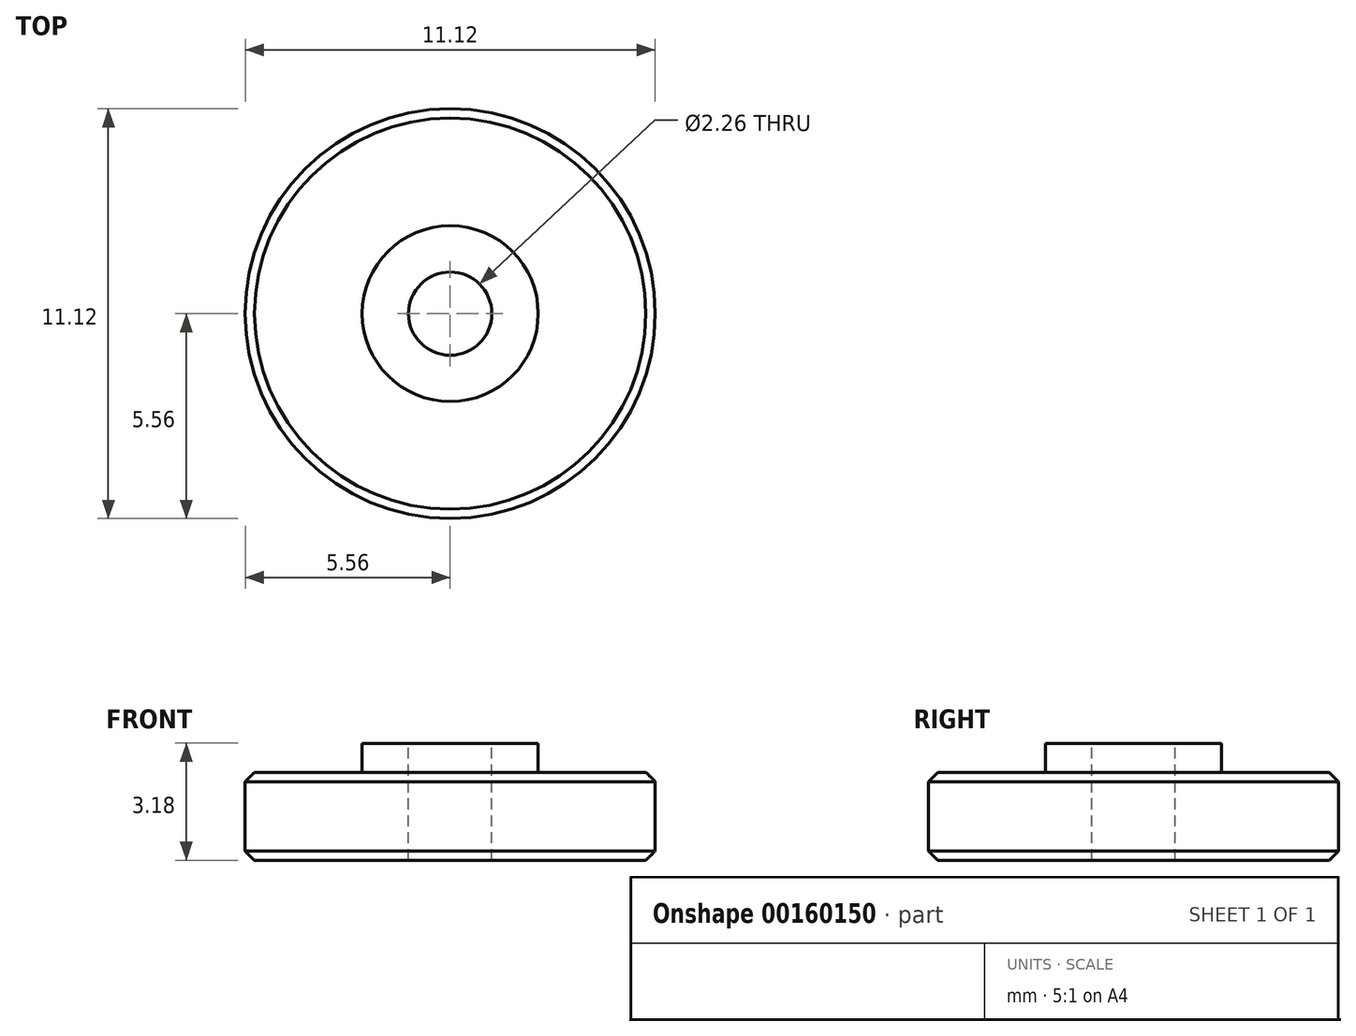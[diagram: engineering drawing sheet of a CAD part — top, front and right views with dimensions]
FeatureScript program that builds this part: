
annotation { "Feature Type Name" : "Feature", "Feature Type Description" : "" }
export const myFeature = defineFeature(function(context is Context, id is Id, definition is map)
    precondition{}
    {
        {
            var Q0;
            Q0=qCreatedBy(makeId("Top.planeOp"),FACE);
            var sketch = newSketch(context, id + "F0", { "sketchPlane" : qUnion([Q0])});
            skCircle(sketch, "E0", {"center": v(0, 0) * mm, "radius": 5.56 * mm});
            skSolve(sketch);
        }
        {
            var Q0;
            Q0 = qSketchRegion(id + "F0", true);
            extrude(context, id + "F1", {"entities" : qUnion([Q0]), "depth" : 2.4 * mm});
        }
        {
            var Q0;
            Q0=makeQuery(id+"F1.opExtrude","CAP_FACE",FACE,{"disambiguationData":[OSD([sQuery(id+"F0.wireOp",EDGE,"E0")])],"isStart":false});
            var sketch = newSketch(context, id + "F2", { "sketchPlane" : qUnion([Q0])});
            skCircle(sketch, "E1", {"center": v(0, 0) * mm, "radius": 2.39 * mm});
            skSolve(sketch);
        }
        {
            var Q0;
            Q0 = qSketchRegion(id + "F2", true);
            extrude(context, id + "F3", {"entities" : qUnion([Q0]), "operationType" : NewBodyOperationType.ADD, "depth" : 0.79 * mm});
        }
        {
            var Q0;
            Q0=makeQuery(id+"F3.opExtrude","CAP_FACE",FACE,{"disambiguationData":[OSD([sQuery(id+"F2.wireOp",EDGE,"E1")])],"isStart":false});
            var sketch = newSketch(context, id + "F4", { "sketchPlane" : qUnion([Q0])});
            skCircle(sketch, "E2", {"center": v(0, 0) * mm, "radius": 1.13 * mm});
            skSolve(sketch);
        }
        {
            var Q0;
            Q0 = qSketchRegion(id + "F4", true);
            extrude(context, id + "F5", {"entities" : qUnion([Q0]), "operationType" : NewBodyOperationType.REMOVE, "endBound" : BoundingType.THROUGH_ALL, "oppositeDirection" : true, "depth" : 25.4 * mm});
        }
        {
            var Q0;
            Q0=makeQuery(id+"F1.opExtrude","CAP_EDGE",EDGE,{"disambiguationData":[OSD([sQuery(id+"F0.wireOp",EDGE,"E0")])],"isStart":false});
            var Q1;
            Q1=makeQuery(id+"F1.opExtrude","CAP_EDGE",EDGE,{"disambiguationData":[OSD([sQuery(id+"F0.wireOp",EDGE,"E0")])],"isStart":true});
            chamfer(context, id + "F6", {"entities" : qUnion([Q0, Q1]), "width" : 0.25 * mm, "tangentPropagation" : true});
        }
    });
